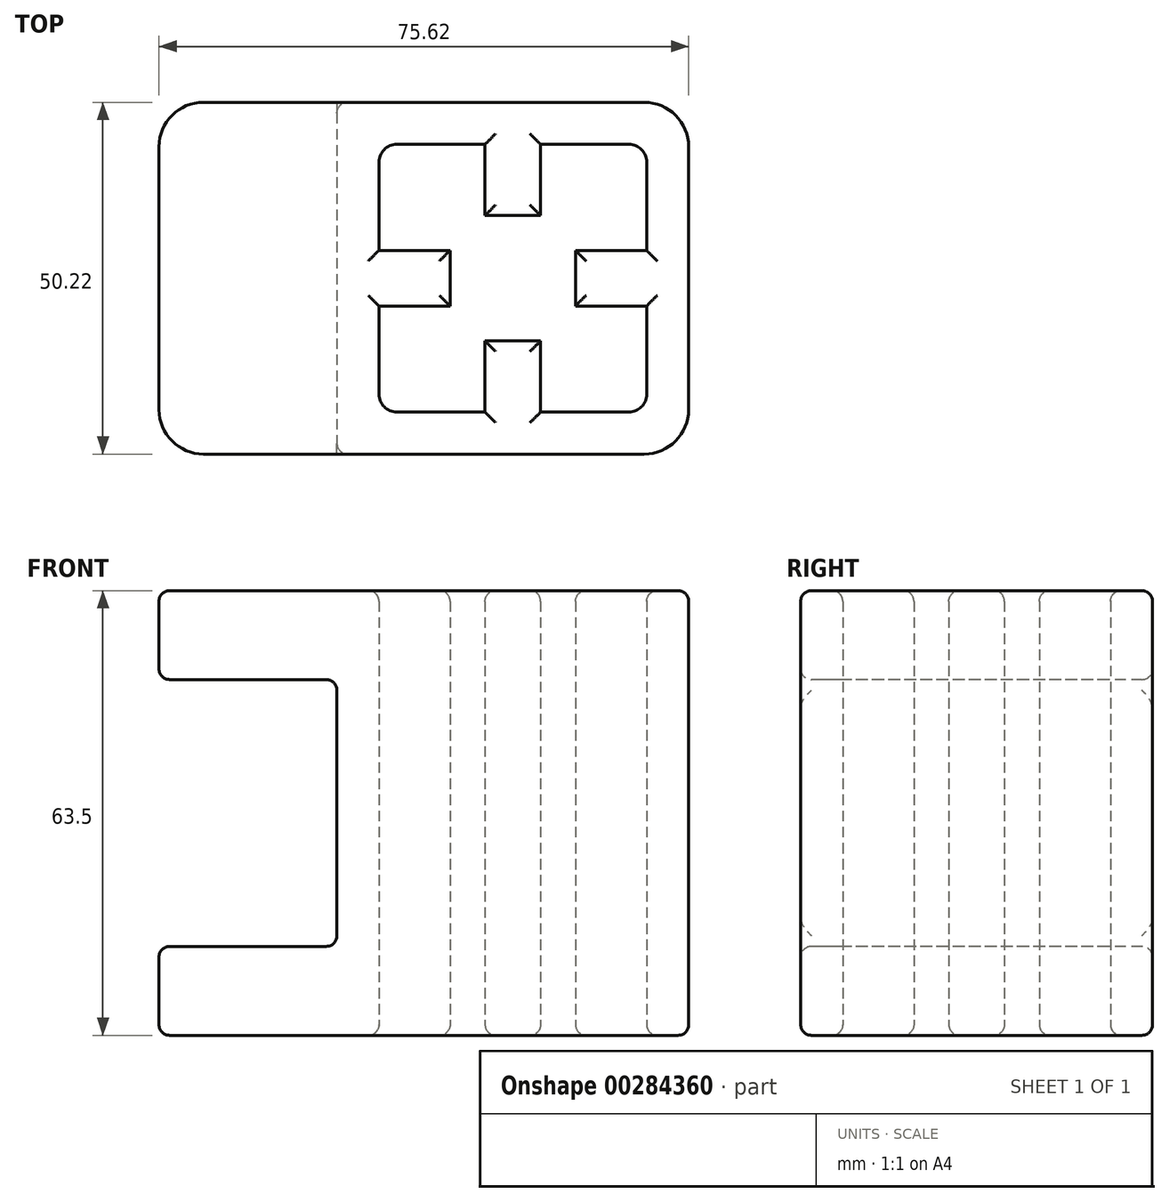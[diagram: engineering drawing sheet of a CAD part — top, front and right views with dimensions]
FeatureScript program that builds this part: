
annotation { "Feature Type Name" : "Feature", "Feature Type Description" : "" }
export const myFeature = defineFeature(function(context is Context, id is Id, definition is map)
    precondition{}
    {
        {
            var Q0;
            Q0=qCreatedBy(makeId("Top.planeOp"),FACE);
            var sketch = newSketch(context, id + "F0", { "sketchPlane" : qUnion([Q0])});
            skLineSegment(sketch, "E0.rect.bottom", {"start": v(16.57, -19.11) * mm, "end": v(3.97, -19.11) * mm});
            skLineSegment(sketch, "E0.rect.top", {"start": v(16.57, 19.11) * mm, "end": v(3.97, 19.11) * mm});
            skLineSegment(sketch, "E0.rect.left", {"start": v(19.11, -16.57) * mm, "end": v(19.11, -3.97) * mm});
            skLineSegment(sketch, "E0.rect.right", {"start": v(-19.11, -16.57) * mm, "end": v(-19.11, -3.97) * mm});
            skPoint(sketch, "E0.rect.middle", {"position": v(0, 0) * mm});
            skLineSegment(sketch, "E1.0", {"start": v(-25.11, -25.11) * mm, "end": v(-25.11, 25.11) * mm});
            skLineSegment(sketch, "E1.1", {"start": v(25.11, -25.11) * mm, "end": v(-25.11, -25.11) * mm});
            skLineSegment(sketch, "E1.2", {"start": v(25.11, -25.11) * mm, "end": v(25.11, 25.11) * mm});
            skLineSegment(sketch, "E1.3", {"start": v(25.11, 25.11) * mm, "end": v(-25.11, 25.11) * mm});
            skLineSegment(sketch, "E2", {"start": v(-3.97, 19.11) * mm, "end": v(-3.97, 8.95) * mm});
            skLineSegment(sketch, "E3", {"start": v(-3.97, 8.95) * mm, "end": v(3.97, 8.95) * mm});
            skLineSegment(sketch, "E4", {"start": v(3.97, 8.95) * mm, "end": v(3.97, 19.11) * mm});
            skPoint(sketch, "E5.orphan", {"position": v(0, 19.11) * mm});
            skPoint(sketch, "E6.end.orphan", {"position": v(0, -19.11) * mm});
            skPoint(sketch, "E7.orphan", {"position": v(-19.11, 0) * mm});
            skPoint(sketch, "E8.start.orphan", {"position": v(19.11, 0) * mm});
            skPoint(sketch, "E9", {"position": v(0, 8.95) * mm});
            skLineSegment(sketch, "E10", {"start": v(0, 0) * mm, "end": v(0, 8.95) * mm});
            skLineSegment(sketch, "E11.1.0", {"start": v(-8.95, 3.97) * mm, "end": v(-19.11, 3.97) * mm});
            skLineSegment(sketch, "E11.1.1", {"start": v(-19.11, -3.97) * mm, "end": v(-8.95, -3.97) * mm});
            skLineSegment(sketch, "E11.1.2", {"start": v(-8.95, -3.97) * mm, "end": v(-8.95, 3.97) * mm});
            skLineSegment(sketch, "E11.2.0", {"start": v(-3.97, -8.95) * mm, "end": v(-3.97, -19.11) * mm});
            skLineSegment(sketch, "E11.2.1", {"start": v(3.97, -19.11) * mm, "end": v(3.97, -8.95) * mm});
            skLineSegment(sketch, "E11.2.2", {"start": v(3.97, -8.95) * mm, "end": v(-3.97, -8.95) * mm});
            skLineSegment(sketch, "E11.3.0", {"start": v(8.95, -3.97) * mm, "end": v(19.11, -3.97) * mm});
            skLineSegment(sketch, "E11.3.1", {"start": v(19.11, 3.97) * mm, "end": v(8.95, 3.97) * mm});
            skLineSegment(sketch, "E11.3.2", {"start": v(8.95, 3.97) * mm, "end": v(8.95, -3.97) * mm});
            skPoint(sketch, "E12.visualSharp", {"position": v(-19.11, 19.11) * mm});
            skArc(sketch, "E12.filletArc", {"start": v(-16.57, 19.11) * mm, "mid": v(-18.37, 18.37) * mm, "end": v(-19.11, 16.57) * mm});
            skPoint(sketch, "E13.visualSharp", {"position": v(19.11, 19.11) * mm});
            skArc(sketch, "E13.filletArc", {"start": v(19.11, 16.57) * mm, "mid": v(18.37, 18.37) * mm, "end": v(16.57, 19.11) * mm});
            skPoint(sketch, "E14.visualSharp", {"position": v(19.11, -19.11) * mm});
            skArc(sketch, "E14.filletArc", {"start": v(16.57, -19.11) * mm, "mid": v(18.37, -18.37) * mm, "end": v(19.11, -16.57) * mm});
            skPoint(sketch, "E15.visualSharp", {"position": v(-19.11, -19.11) * mm});
            skArc(sketch, "E15.filletArc", {"start": v(-19.11, -16.57) * mm, "mid": v(-18.37, -18.37) * mm, "end": v(-16.57, -19.11) * mm});
            skLineSegment(sketch, "E16.trimOffspring", {"start": v(-19.11, 3.97) * mm, "end": v(-19.11, 16.57) * mm});
            skLineSegment(sketch, "E17.trimOffspring", {"start": v(-3.97, -19.11) * mm, "end": v(-16.57, -19.11) * mm});
            skLineSegment(sketch, "E18.trimOffspring", {"start": v(19.11, 3.97) * mm, "end": v(19.11, 16.57) * mm});
            skLineSegment(sketch, "E19.trimOffspring", {"start": v(-3.97, 19.11) * mm, "end": v(-16.57, 19.11) * mm});
            skPoint(sketch, "E20.visualSharp", {"position": v(-25.11, 25.11) * mm});
            skLineSegment(sketch, "E20.filletArc", {"start": v(-25.11, 25.11) * mm, "end": v(-25.11, 25.11) * mm});
            skPoint(sketch, "E21.visualSharp", {"position": v(25.11, 25.11) * mm});
            skPoint(sketch, "E22.visualSharp", {"position": v(25.11, -25.11) * mm});
            skPoint(sketch, "E23.visualSharp", {"position": v(-25.11, -25.11) * mm});
            skLineSegment(sketch, "E23.filletArc", {"start": v(-25.11, -25.11) * mm, "end": v(-25.11, -25.11) * mm});
            skLineSegment(sketch, "E24.filletArc", {"start": v(25.11, 25.11) * mm, "end": v(25.11, 25.11) * mm});
            skLineSegment(sketch, "E25.filletArc", {"start": v(25.11, -25.11) * mm, "end": v(25.11, -25.11) * mm});
            skSolve(sketch);
        }
        {
            var Q0;
            Q0=qSketchRegion(id+"F0",true);
            extrude(context, id + "F1", {"entities" : qUnion([Q0]), "depth" : 63.5 * mm});
        }
        {
            var Q0;
            Q0=makeQuery(id+"F1.opExtrude","SWEPT_FACE",FACE,{"disambiguationData":[OSD([sQuery(id+"F0.wireOp",EDGE,"E1.0")])]});
            var sketch = newSketch(context, id + "F2", { "sketchPlane" : qUnion([Q0])});
            skLineSegment(sketch, "E26.bottom", {"start": v(-25.11, 0) * mm, "end": v(25.11, 0) * mm});
            skLineSegment(sketch, "E26.top", {"start": v(-25.11, 12.7) * mm, "end": v(25.11, 12.7) * mm});
            skLineSegment(sketch, "E26.left", {"start": v(-25.11, 0) * mm, "end": v(-25.11, 12.7) * mm});
            skLineSegment(sketch, "E26.right", {"start": v(25.11, 0) * mm, "end": v(25.11, 12.7) * mm});
            skLineSegment(sketch, "E27", {"start": v(-25.11, 31.75) * mm, "end": v(25.11, 31.75) * mm, "construction": true});
            skLineSegment(sketch, "E28.MirrorCS", {"start": v(25.11, 63.5) * mm, "end": v(25.11, 50.8) * mm});
            skLineSegment(sketch, "E29.MirrorCS", {"start": v(-25.11, 63.5) * mm, "end": v(-25.11, 50.8) * mm});
            skLineSegment(sketch, "E30.MirrorCS", {"start": v(-25.11, 63.5) * mm, "end": v(25.11, 63.5) * mm});
            skLineSegment(sketch, "E31.MirrorCS", {"start": v(-25.11, 50.8) * mm, "end": v(25.11, 50.8) * mm});
            skSolve(sketch);
        }
        {
            var Q0;
            Q0=makeQuery(id+"F2.imprint","IMPRINT",FACE,{"disambiguationData":[TD([[makeQuery(id+"F2.imprint","IMPRINT",EDGE,{"derivedFrom":sQuery(id+"F2.wireOp",EDGE,"E26.bottom")}),-1.0]])]});
            var Q1;
            Q1=makeQuery(id+"F2.imprint","IMPRINT",FACE,{"disambiguationData":[TD([[makeQuery(id+"F2.imprint","IMPRINT",EDGE,{"derivedFrom":sQuery(id+"F2.wireOp",EDGE,"E30.MirrorCS")}),1.0]])]});
            extrude(context, id + "F3", {"entities" : qUnion([Q0, Q1]), "operationType" : NewBodyOperationType.ADD, "depth" : 25.4 * mm});
        }
        {
            var Q0;
            Q0=makeQuery(id+"F3.opExtrude","CAP_EDGE",EDGE,{"disambiguationData":[OSD([sQuery(id+"F2.wireOp",EDGE,"E26.top")])],"isStart":true});
            var Q1;
            Q1=makeQuery(id+"F3.opExtrude","CAP_EDGE",EDGE,{"disambiguationData":[OSD([sQuery(id+"F2.wireOp",EDGE,"E31.MirrorCS")])],"isStart":true});
            var Q2;
            Q2=makeQuery(id+"F3.opExtrude","CAP_EDGE",EDGE,{"disambiguationData":[OSD([sQuery(id+"F2.wireOp",EDGE,"E26.right")])],"isStart":false});
            var Q3;
            Q3=makeQuery(id+"F3.opExtrude","CAP_EDGE",EDGE,{"disambiguationData":[OSD([sQuery(id+"F2.wireOp",EDGE,"E26.left")])],"isStart":false});
            var Q4;
            Q4=makeQuery(id+"F3.opExtrude","CAP_EDGE",EDGE,{"disambiguationData":[OSD([sQuery(id+"F2.wireOp",EDGE,"E29.MirrorCS")])],"isStart":false});
            var Q5;
            Q5=makeQuery(id+"F3.opExtrude","CAP_EDGE",EDGE,{"disambiguationData":[OSD([sQuery(id+"F2.wireOp",EDGE,"E28.MirrorCS")])],"isStart":false});
            var Q6;
            Q6=makeQuery(id+"F1.opExtrude","SWEPT_EDGE",EDGE,{"disambiguationData":[OSD([sQuery(id+"F0.wireOp",EDGE,"E1.1"),sQuery(id+"F0.wireOp",EDGE,"E1.2")])]});
            var Q7;
            Q7=makeQuery(id+"F1.opExtrude","SWEPT_EDGE",EDGE,{"disambiguationData":[OSD([sQuery(id+"F0.wireOp",EDGE,"E1.2"),sQuery(id+"F0.wireOp",EDGE,"E1.3")])]});
            fillet(context, id + "F4", {"entities" : qUnion([Q0, Q1, Q2, Q3, Q4, Q5, Q6, Q7]), "radius" : 6.35 * mm, "tangentPropagation" : true, "allowEdgeOverflow" : false});
        }
        {
            var Q0;
            Q0=makeQuery(id+"F3.boolean.opBoolean","MERGE",FACE,{"derivedFrom":[makeQuery(id+"F1.opExtrude","CAP_FACE",FACE,{"disambiguationData":[OSD([sQuery(id+"F0.wireOp",EDGE,"E0.rect.bottom"),sQuery(id+"F0.wireOp",EDGE,"E0.rect.top"),sQuery(id+"F0.wireOp",EDGE,"E0.rect.left"),sQuery(id+"F0.wireOp",EDGE,"E0.rect.right"),sQuery(id+"F0.wireOp",EDGE,"E1.0"),sQuery(id+"F0.wireOp",EDGE,"E1.1"),sQuery(id+"F0.wireOp",EDGE,"E1.2"),sQuery(id+"F0.wireOp",EDGE,"E1.3"),sQuery(id+"F0.wireOp",EDGE,"E2"),sQuery(id+"F0.wireOp",EDGE,"E3"),sQuery(id+"F0.wireOp",EDGE,"E4"),sQuery(id+"F0.wireOp",EDGE,"E11.1.0"),sQuery(id+"F0.wireOp",EDGE,"E11.1.1"),sQuery(id+"F0.wireOp",EDGE,"E11.1.2"),sQuery(id+"F0.wireOp",EDGE,"E11.2.0"),sQuery(id+"F0.wireOp",EDGE,"E11.2.1"),sQuery(id+"F0.wireOp",EDGE,"E11.2.2"),sQuery(id+"F0.wireOp",EDGE,"E11.3.0"),sQuery(id+"F0.wireOp",EDGE,"E11.3.1"),sQuery(id+"F0.wireOp",EDGE,"E11.3.2"),sQuery(id+"F0.wireOp",EDGE,"E12.filletArc"),sQuery(id+"F0.wireOp",EDGE,"E13.filletArc"),sQuery(id+"F0.wireOp",EDGE,"E14.filletArc"),sQuery(id+"F0.wireOp",EDGE,"E15.filletArc"),sQuery(id+"F0.wireOp",EDGE,"E16.trimOffspring"),sQuery(id+"F0.wireOp",EDGE,"E17.trimOffspring"),sQuery(id+"F0.wireOp",EDGE,"E18.trimOffspring"),sQuery(id+"F0.wireOp",EDGE,"E19.trimOffspring")])],"isStart":true}),makeQuery(id+"F3.opExtrude","SWEPT_FACE",FACE,{"disambiguationData":[OSD([sQuery(id+"F2.wireOp",EDGE,"E26.bottom")])]})]});
            var Q1;
            Q1=makeQuery(id+"F3.boolean.opBoolean","MERGE",FACE,{"derivedFrom":[makeQuery(id+"F1.opExtrude","CAP_FACE",FACE,{"disambiguationData":[OSD([sQuery(id+"F0.wireOp",EDGE,"E0.rect.bottom"),sQuery(id+"F0.wireOp",EDGE,"E0.rect.top"),sQuery(id+"F0.wireOp",EDGE,"E0.rect.left"),sQuery(id+"F0.wireOp",EDGE,"E0.rect.right"),sQuery(id+"F0.wireOp",EDGE,"E1.0"),sQuery(id+"F0.wireOp",EDGE,"E1.1"),sQuery(id+"F0.wireOp",EDGE,"E1.2"),sQuery(id+"F0.wireOp",EDGE,"E1.3"),sQuery(id+"F0.wireOp",EDGE,"E2"),sQuery(id+"F0.wireOp",EDGE,"E3"),sQuery(id+"F0.wireOp",EDGE,"E4"),sQuery(id+"F0.wireOp",EDGE,"E11.1.0"),sQuery(id+"F0.wireOp",EDGE,"E11.1.1"),sQuery(id+"F0.wireOp",EDGE,"E11.1.2"),sQuery(id+"F0.wireOp",EDGE,"E11.2.0"),sQuery(id+"F0.wireOp",EDGE,"E11.2.1"),sQuery(id+"F0.wireOp",EDGE,"E11.2.2"),sQuery(id+"F0.wireOp",EDGE,"E11.3.0"),sQuery(id+"F0.wireOp",EDGE,"E11.3.1"),sQuery(id+"F0.wireOp",EDGE,"E11.3.2"),sQuery(id+"F0.wireOp",EDGE,"E12.filletArc"),sQuery(id+"F0.wireOp",EDGE,"E13.filletArc"),sQuery(id+"F0.wireOp",EDGE,"E14.filletArc"),sQuery(id+"F0.wireOp",EDGE,"E15.filletArc"),sQuery(id+"F0.wireOp",EDGE,"E16.trimOffspring"),sQuery(id+"F0.wireOp",EDGE,"E17.trimOffspring"),sQuery(id+"F0.wireOp",EDGE,"E18.trimOffspring"),sQuery(id+"F0.wireOp",EDGE,"E19.trimOffspring")])],"isStart":false}),makeQuery(id+"F3.opExtrude","SWEPT_FACE",FACE,{"disambiguationData":[OSD([sQuery(id+"F2.wireOp",EDGE,"E30.MirrorCS")])]})]});
            var Q2;
            Q2=makeQuery(id+"F3.opExtrude","SWEPT_FACE",FACE,{"disambiguationData":[OSD([sQuery(id+"F2.wireOp",EDGE,"E31.MirrorCS")])]});
            var Q3;
            Q3=makeQuery(id+"F3.opExtrude","SWEPT_FACE",FACE,{"disambiguationData":[OSD([sQuery(id+"F2.wireOp",EDGE,"E26.top")])]});
            fillet(context, id + "F5", {"entities" : qUnion([Q0, Q1, Q2, Q3]), "radius" : 1.52 * mm, "tangentPropagation" : true, "allowEdgeOverflow" : false});
        }
    });
